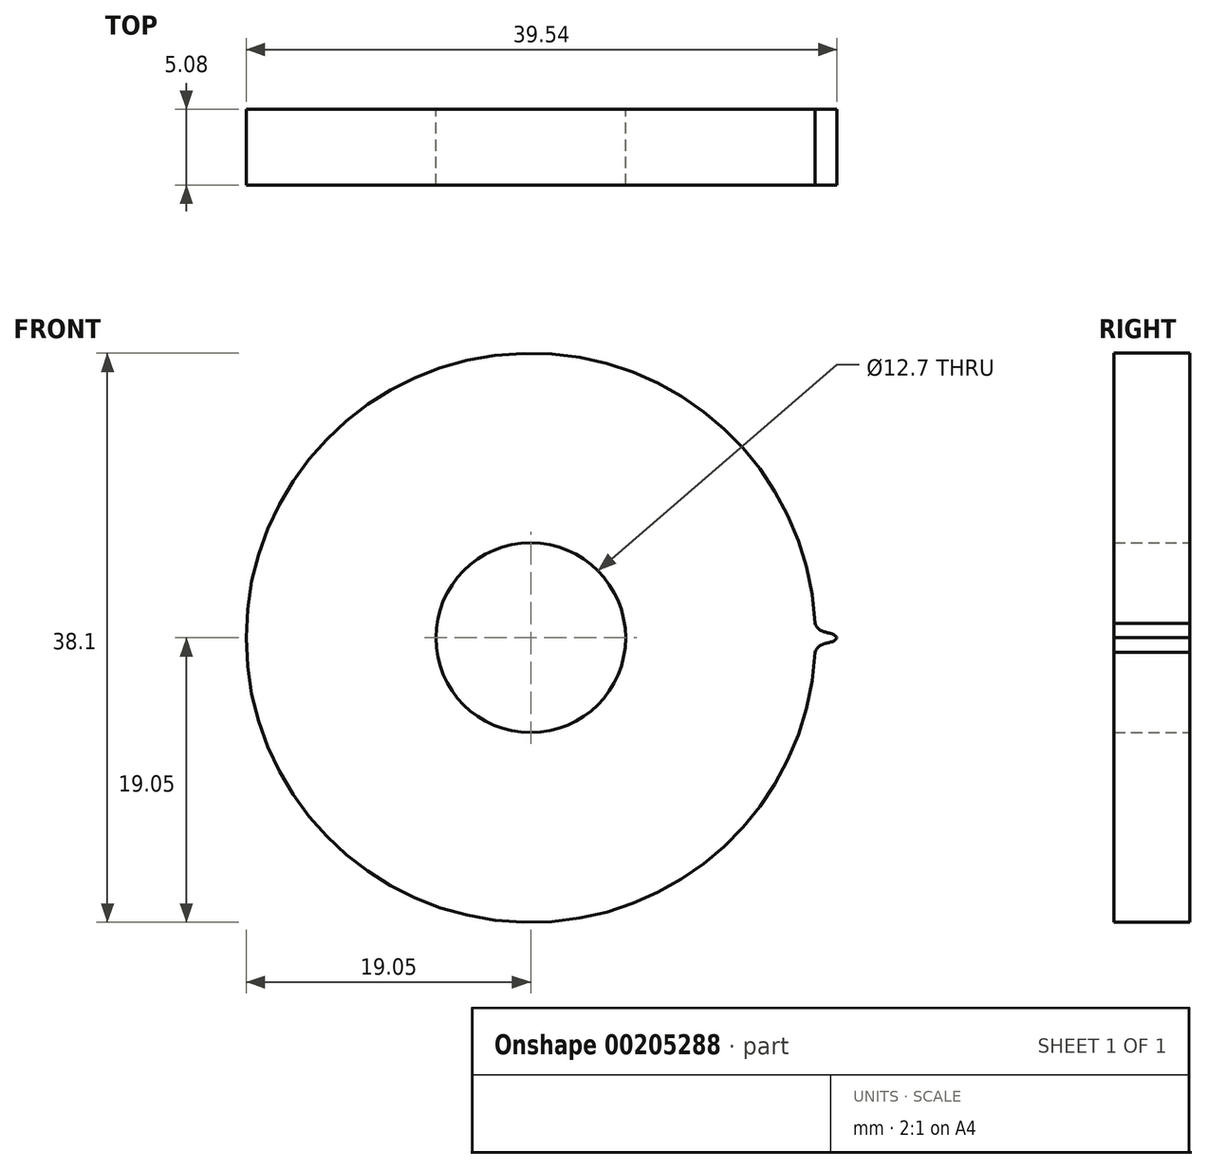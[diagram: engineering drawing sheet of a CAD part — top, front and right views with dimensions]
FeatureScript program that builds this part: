
annotation { "Feature Type Name" : "Feature", "Feature Type Description" : "" }
export const myFeature = defineFeature(function(context is Context, id is Id, definition is map)
    precondition{}
    {
        {
            var Q0;
            Q0=qCreatedBy(makeId("Front.planeOp"),FACE);
            var sketch = newSketch(context, id + "F0", { "sketchPlane" : qUnion([Q0])});
            skCircle(sketch, "E0", {"center": v(0, 0) * mm, "radius": 6.35 * mm});
            skCircle(sketch, "E1", {"center": v(0, 0) * mm, "radius": 19.05 * mm});
            skFitSpline(sketch, "E2", {"points": [v(19.02, 0.98) * mm, v(20.49, 0) * mm], "startDerivative": vector(0.9, -2.52) * mm, "endDerivative": vector(0.9, -1.58) * mm});
            skFitSpline(sketch, "E3.MirrorCS", {"points": [v(19.02, -0.98) * mm, v(20.49, 0) * mm], "startDerivative": vector(0.9, 2.52) * mm, "endDerivative": vector(0.9, 1.58) * mm});
            skSolve(sketch);
        }
        {
            var Q0;
            Q0 = qSketchRegion(id + "F0", true);
            extrude(context, id + "F1", {"entities" : qUnion([Q0]), "endBound" : BoundingType.SYMMETRIC, "depth" : 5.08 * mm});
        }
    });
